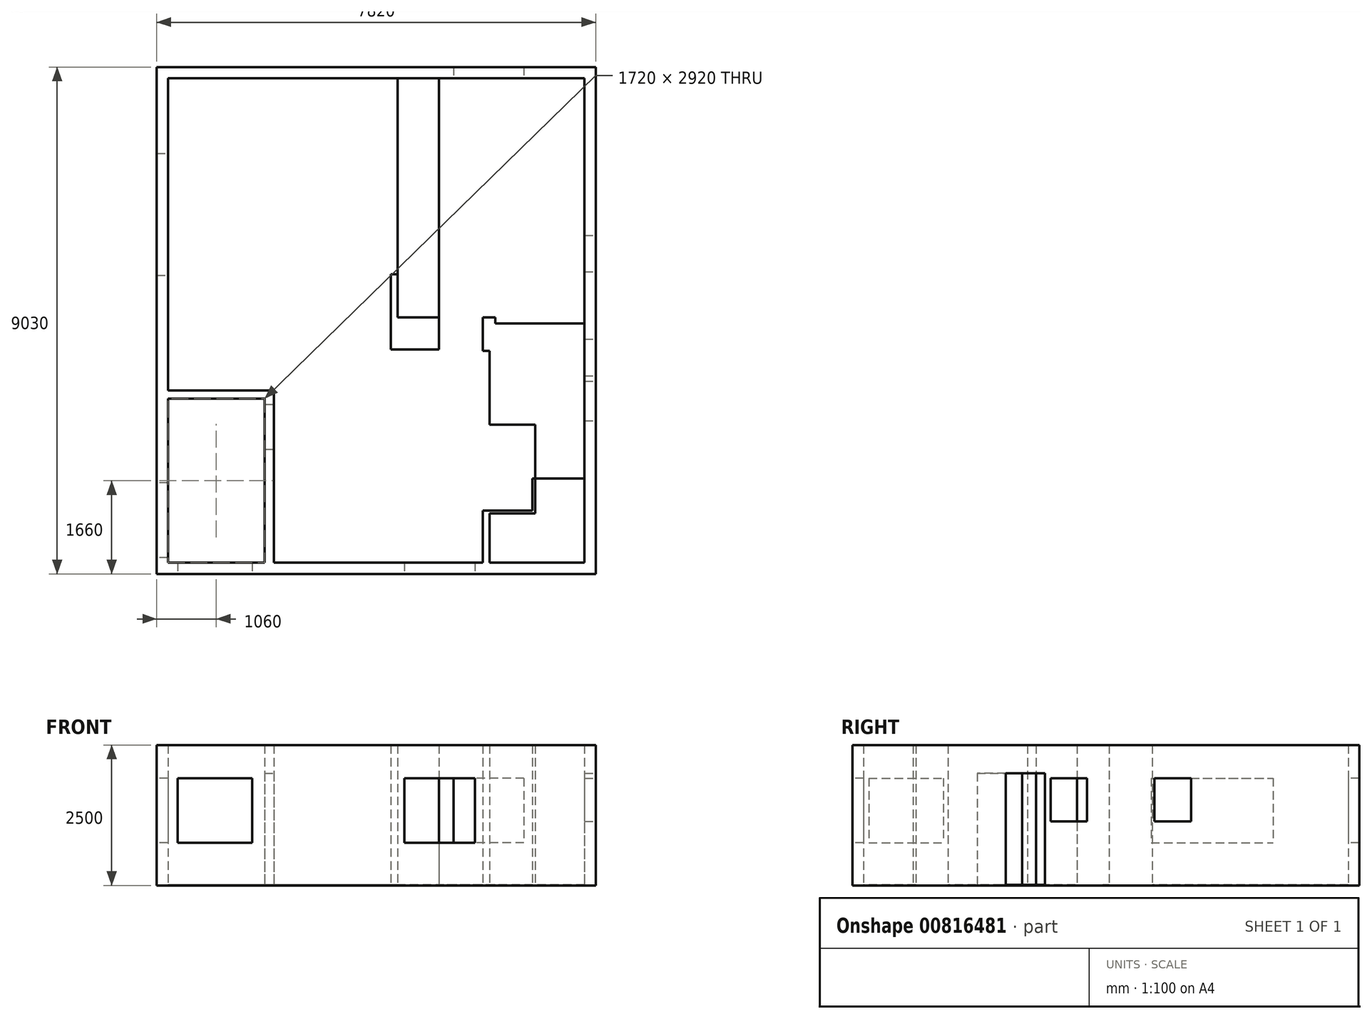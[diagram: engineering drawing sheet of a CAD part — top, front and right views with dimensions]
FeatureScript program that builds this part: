
annotation { "Feature Type Name" : "Feature", "Feature Type Description" : "" }
export const myFeature = defineFeature(function(context is Context, id is Id, definition is map)
    precondition{}
    {
        {
            var Q0;
            Q0=qCreatedBy(makeId("Top.planeOp"),FACE);
            var sketch = newSketch(context, id + "F0", { "sketchPlane" : qUnion([Q0])});
            skLineSegment(sketch, "E0.bottom", {"start": v(3710, -4315) * mm, "end": v(-3710, -4315) * mm});
            skLineSegment(sketch, "E0.top", {"start": v(3710, 4315) * mm, "end": v(-3710, 4315) * mm});
            skLineSegment(sketch, "E0.left", {"start": v(3710, -4315) * mm, "end": v(3710, 4315) * mm});
            skLineSegment(sketch, "E0.right", {"start": v(-3710, -4315) * mm, "end": v(-3710, 4315) * mm});
            skPoint(sketch, "E0.middle", {"position": v(0, 0) * mm});
            skLineSegment(sketch, "E1.0", {"start": v(3910, 4515) * mm, "end": v(-3910, 4515) * mm});
            skLineSegment(sketch, "E1.1", {"start": v(3910, -4515) * mm, "end": v(3910, 4515) * mm});
            skLineSegment(sketch, "E1.2", {"start": v(3910, -4515) * mm, "end": v(-3910, -4515) * mm});
            skLineSegment(sketch, "E1.3", {"start": v(-3910, -4515) * mm, "end": v(-3910, 4515) * mm});
            skLineSegment(sketch, "E2", {"start": v(380, 4315) * mm, "end": v(380, -515) * mm});
            skLineSegment(sketch, "E3", {"start": v(380, -515) * mm, "end": v(-3710, -515) * mm});
            skLineSegment(sketch, "E4.0", {"start": v(260, 4315) * mm, "end": v(260, -395) * mm});
            skLineSegment(sketch, "E5.0", {"start": v(260, -395) * mm, "end": v(-3710, -395) * mm});
            skLineSegment(sketch, "E6", {"start": v(3710, 55) * mm, "end": v(1900, 55) * mm});
            skLineSegment(sketch, "E7.0", {"start": v(3710, -55) * mm, "end": v(2020, -55) * mm});
            skLineSegment(sketch, "E8", {"start": v(2120, 105) * mm, "end": v(2120, -105) * mm});
            skLineSegment(sketch, "E9.0", {"start": v(2940, 105) * mm, "end": v(2940, -105) * mm});
            skLineSegment(sketch, "E10", {"start": v(3660, 865) * mm, "end": v(3960, 865) * mm});
            skLineSegment(sketch, "E11.0", {"start": v(3660, 1515) * mm, "end": v(3960, 1515) * mm});
            skLineSegment(sketch, "E12", {"start": v(2630, 4565) * mm, "end": v(2630, 4265) * mm});
            skLineSegment(sketch, "E13.0", {"start": v(1380, 4565) * mm, "end": v(1380, 4265) * mm});
            skLineSegment(sketch, "E14", {"start": v(210, 1645) * mm, "end": v(430, 1645) * mm});
            skLineSegment(sketch, "E15.0", {"start": v(210, 825) * mm, "end": v(430, 825) * mm});
            skLineSegment(sketch, "E16", {"start": v(3660, -335) * mm, "end": v(3960, -335) * mm});
            skLineSegment(sketch, "E17.0", {"start": v(3660, -985) * mm, "end": v(3960, -985) * mm});
            skLineSegment(sketch, "E18.0", {"start": v(3660, -1085) * mm, "end": v(3960, -1085) * mm});
            skLineSegment(sketch, "E19.0", {"start": v(3660, -1785) * mm, "end": v(3960, -1785) * mm});
            skLineSegment(sketch, "E20", {"start": v(3710, -2815) * mm, "end": v(2830, -2815) * mm});
            skLineSegment(sketch, "E21", {"start": v(2830, -2815) * mm, "end": v(2830, -3435) * mm});
            skLineSegment(sketch, "E22", {"start": v(-3960, 2975) * mm, "end": v(-3660, 2975) * mm});
            skLineSegment(sketch, "E23.0", {"start": v(-3960, 805) * mm, "end": v(-3660, 805) * mm});
            skLineSegment(sketch, "E24", {"start": v(-1560, -345) * mm, "end": v(-1560, -565) * mm});
            skLineSegment(sketch, "E25.0", {"start": v(-740, -345) * mm, "end": v(-740, -565) * mm});
            skLineSegment(sketch, "E26", {"start": v(-1820, -515) * mm, "end": v(-1820, -4315) * mm});
            skLineSegment(sketch, "E27", {"start": v(-3710, -1245) * mm, "end": v(-1820, -1245) * mm});
            skLineSegment(sketch, "E28.0", {"start": v(-3710, -1395) * mm, "end": v(-1990, -1395) * mm});
            skLineSegment(sketch, "E29", {"start": v(-3660, -2895) * mm, "end": v(-3960, -2895) * mm});
            skLineSegment(sketch, "E30.0", {"start": v(-3660, -4225) * mm, "end": v(-3960, -4225) * mm});
            skLineSegment(sketch, "E31", {"start": v(-2210, -4265) * mm, "end": v(-2210, -4565) * mm});
            skLineSegment(sketch, "E32.0", {"start": v(-3540, -4265) * mm, "end": v(-3540, -4565) * mm});
            skLineSegment(sketch, "E33", {"start": v(-1990, -4315) * mm, "end": v(-1990, -1395) * mm});
            skLineSegment(sketch, "E34", {"start": v(-1920, -515) * mm, "end": v(-1920, -1245) * mm});
            skLineSegment(sketch, "E35", {"start": v(-2040, -1495) * mm, "end": v(-1770, -1495) * mm});
            skLineSegment(sketch, "E36.0", {"start": v(-2040, -2295) * mm, "end": v(-1770, -2295) * mm});
            skLineSegment(sketch, "E37", {"start": v(-1770, -535) * mm, "end": v(-1970, -535) * mm});
            skLineSegment(sketch, "E38.0", {"start": v(-1770, -1135) * mm, "end": v(-1970, -1135) * mm});
            skLineSegment(sketch, "E39", {"start": v(2020, -55) * mm, "end": v(2020, -515) * mm});
            skLineSegment(sketch, "E40", {"start": v(1900, -515) * mm, "end": v(380, -515) * mm});
            skLineSegment(sketch, "E41", {"start": v(500, -4265) * mm, "end": v(500, -4565) * mm});
            skLineSegment(sketch, "E42.0", {"start": v(1760, -4265) * mm, "end": v(1760, -4565) * mm});
            skLineSegment(sketch, "E43", {"start": v(2020, -515) * mm, "end": v(2020, -4315) * mm});
            skLineSegment(sketch, "E44", {"start": v(2830, -3435) * mm, "end": v(2020, -3435) * mm});
            skLineSegment(sketch, "E45", {"start": v(2830, -3125) * mm, "end": v(3710, -3125) * mm});
            skLineSegment(sketch, "E46", {"start": v(2830, -3435) * mm, "end": v(3710, -3435) * mm});
            skLineSegment(sketch, "E47", {"start": v(2830, -3435) * mm, "end": v(2830, -4315) * mm});
            skLineSegment(sketch, "E48", {"start": v(2425, -3435) * mm, "end": v(2425, -4315) * mm});
            skLineSegment(sketch, "E49", {"start": v(2830, -3435) * mm, "end": v(3710, -4315) * mm});
            skLineSegment(sketch, "E50", {"start": v(2830, -3435) * mm, "end": v(3710, -3799.5) * mm});
            skLineSegment(sketch, "E51", {"start": v(2830, -3435) * mm, "end": v(3194.5, -4315) * mm});
            skLineSegment(sketch, "E52", {"start": v(1900, -4315) * mm, "end": v(1900, 55) * mm});
            skLineSegment(sketch, "E53", {"start": v(1850, -1365) * mm, "end": v(2070, -1365) * mm});
            skLineSegment(sketch, "E54.0", {"start": v(1850, -545) * mm, "end": v(2070, -545) * mm});
            skLineSegment(sketch, "E55", {"start": v(2020, -1855) * mm, "end": v(2830, -1855) * mm});
            skLineSegment(sketch, "E56", {"start": v(2830, -1855) * mm, "end": v(2830, -2815) * mm});
            skLineSegment(sketch, "E57.0", {"start": v(2020, -1905) * mm, "end": v(2780, -1905) * mm});
            skLineSegment(sketch, "E58.0", {"start": v(2780, -3385) * mm, "end": v(2020, -3385) * mm});
            skLineSegment(sketch, "E59", {"start": v(2780, -1905) * mm, "end": v(2780, -3385) * mm});
            skLineSegment(sketch, "E60", {"start": v(2880, -2565) * mm, "end": v(2730, -2565) * mm});
            skLineSegment(sketch, "E61.0", {"start": v(2880, -1915) * mm, "end": v(2730, -1915) * mm});
            skLineSegment(sketch, "E62", {"start": v(1900, -415) * mm, "end": v(1120, -415) * mm});
            skLineSegment(sketch, "E63.trimOffspring", {"start": v(1120, 55) * mm, "end": v(380, 55) * mm});
            skLineSegment(sketch, "E64", {"start": v(1120, 55) * mm, "end": v(1120, -515) * mm});
            skLineSegment(sketch, "E65", {"start": v(2830, -2815) * mm, "end": v(2780, -2815) * mm});
            skLineSegment(sketch, "E66", {"start": v(2020, -3385) * mm, "end": v(1900, -3385) * mm});
            skLineSegment(sketch, "E67", {"start": v(260, -395) * mm, "end": v(260, -515) * mm});
            skLineSegment(sketch, "E68", {"start": v(1120, 55) * mm, "end": v(1120, 4315) * mm});
            skSolve(sketch);
        }
        {
            var Q0;
            {var subQ0=sQuery(id+"F0.wireOp",EDGE,"E0.right");var subQ1=sQuery(id+"F0.wireOp",EDGE,"E0.top");var subQ2=makeQuery(id+"F0.imprint","INTERSECT",VERTEX,{"derivedFrom":[subQ1,subQ0]});Q0=makeQuery(id+"F0.imprint","IMPRINT",FACE,{"disambiguationData":[TD([[makeQuery(id+"F0.imprint","IMPRINT",EDGE,{"disambiguationData":[TD([[subQ2,1.0]])],"derivedFrom":subQ1}),1.0]])]});}
            var Q1;
            {var subQ0=sQuery(id+"F0.wireOp",EDGE,"E25.0");var subQ1=sQuery(id+"F0.wireOp",EDGE,"E3");var subQ2=makeQuery(id+"F0.imprint","INTERSECT",VERTEX,{"derivedFrom":[subQ1,subQ0]});Q1=makeQuery(id+"F0.imprint","IMPRINT",FACE,{"disambiguationData":[TD([[makeQuery(id+"F0.imprint","IMPRINT",EDGE,{"disambiguationData":[TD([[subQ2,-1.0]])],"derivedFrom":subQ1}),-1.0]])]});}
            var Q2;
            {var subQ1=sQuery(id+"F0.wireOp",EDGE,"E3");var subQ5=sQuery(id+"F0.wireOp",EDGE,"E0.right");var subQ9=makeQuery(id+"F0.imprint","INTERSECT",VERTEX,{"derivedFrom":[subQ5,subQ1]});Q2=makeQuery(id+"F0.imprint","IMPRINT",FACE,{"disambiguationData":[TD([[makeQuery(id+"F0.imprint","IMPRINT",EDGE,{"disambiguationData":[TD([[subQ9,1.0]])],"derivedFrom":subQ5}),-1.0]])]});}
            var Q3;
            {var subQ9=sQuery(id+"F0.wireOp",EDGE,"E52");var subQ12=sQuery(id+"F0.wireOp",EDGE,"E0.bottom");var subQ18=makeQuery(id+"F0.imprint","INTERSECT",VERTEX,{"derivedFrom":[subQ12,subQ9]});Q3=makeQuery(id+"F0.imprint","IMPRINT",FACE,{"disambiguationData":[TD([[makeQuery(id+"F0.imprint","IMPRINT",EDGE,{"disambiguationData":[TD([[subQ18,-1.0]])],"derivedFrom":subQ12}),-1.0]])]});}
            var Q4;
            {var subQ0=sQuery(id+"F0.wireOp",EDGE,"E35");var subQ1=sQuery(id+"F0.wireOp",EDGE,"E26");var subQ2=makeQuery(id+"F0.imprint","INTERSECT",VERTEX,{"derivedFrom":[subQ1,subQ0]});Q4=makeQuery(id+"F0.imprint","IMPRINT",FACE,{"disambiguationData":[TD([[makeQuery(id+"F0.imprint","IMPRINT",EDGE,{"disambiguationData":[TD([[subQ2,-1.0]])],"derivedFrom":subQ1}),-1.0]])]});}
            var Q5;
            {var subQ5=sQuery(id+"F0.wireOp",EDGE,"E28.0");Q5=makeQuery(id+"F0.imprint","IMPRINT",FACE,{"disambiguationData":[TD([[makeQuery(id+"F0.imprint","IMPRINT",EDGE,{"derivedFrom":subQ5}),-1.0]])]});}
            var Q6;
            {var subQ0=sQuery(id+"F0.wireOp",EDGE,"E54.0");var subQ1=sQuery(id+"F0.wireOp",EDGE,"E43");var subQ2=makeQuery(id+"F0.imprint","INTERSECT",VERTEX,{"derivedFrom":[subQ1,subQ0]});Q6=makeQuery(id+"F0.imprint","IMPRINT",FACE,{"disambiguationData":[TD([[makeQuery(id+"F0.imprint","IMPRINT",EDGE,{"disambiguationData":[TD([[subQ2,-1.0]])],"derivedFrom":subQ1}),-1.0]])]});}
            var Q7;
            {var subQ0=sQuery(id+"F0.wireOp",EDGE,"E20");Q7=makeQuery(id+"F0.imprint","IMPRINT",FACE,{"disambiguationData":[TD([[makeQuery(id+"F0.imprint","IMPRINT",EDGE,{"derivedFrom":subQ0}),-1.0]])]});}
            var Q8;
            {var subQ1=sQuery(id+"F0.wireOp",EDGE,"E57.0");Q8=makeQuery(id+"F0.imprint","IMPRINT",FACE,{"disambiguationData":[TD([[makeQuery(id+"F0.imprint","IMPRINT",EDGE,{"derivedFrom":subQ1}),-1.0]])]});}
            var Q9;
            {var subQ0=sQuery(id+"F0.wireOp",EDGE,"E9.0");var subQ1=sQuery(id+"F0.wireOp",EDGE,"E6");var subQ2=makeQuery(id+"F0.imprint","INTERSECT",VERTEX,{"derivedFrom":[subQ1,subQ0]});Q9=makeQuery(id+"F0.imprint","IMPRINT",FACE,{"disambiguationData":[TD([[makeQuery(id+"F0.imprint","IMPRINT",EDGE,{"disambiguationData":[TD([[subQ2,-1.0]])],"derivedFrom":subQ1}),1.0]])]});}
            var Q10;
            {var subQ0=sQuery(id+"F0.wireOp",EDGE,"E19.0");var subQ1=sQuery(id+"F0.wireOp",EDGE,"E0.left");var subQ2=makeQuery(id+"F0.imprint","INTERSECT",VERTEX,{"derivedFrom":[subQ1,subQ0]});Q10=makeQuery(id+"F0.imprint","IMPRINT",FACE,{"disambiguationData":[TD([[makeQuery(id+"F0.imprint","IMPRINT",EDGE,{"disambiguationData":[TD([[subQ2,-1.0]])],"derivedFrom":subQ1}),-1.0]])]});}
            var Q11;
            {var subQ18=sQuery(id+"F0.wireOp",EDGE,"E62");Q11=makeQuery(id+"F0.imprint","IMPRINT",FACE,{"disambiguationData":[TD([[makeQuery(id+"F0.imprint","IMPRINT",EDGE,{"derivedFrom":subQ18}),-1.0]])]});}
            var Q12;
            {var subQ0=sQuery(id+"F0.wireOp",EDGE,"E14");var subQ1=sQuery(id+"F0.wireOp",EDGE,"E2");var subQ2=makeQuery(id+"F0.imprint","INTERSECT",VERTEX,{"derivedFrom":[subQ1,subQ0]});Q12=makeQuery(id+"F0.imprint","IMPRINT",FACE,{"disambiguationData":[TD([[makeQuery(id+"F0.imprint","IMPRINT",EDGE,{"disambiguationData":[TD([[subQ2,-1.0]])],"derivedFrom":subQ1}),-1.0]])]});}
            var Q13;
            {var subQ0=sQuery(id+"F0.wireOp",EDGE,"E20");Q13=makeQuery(id+"F0.imprint","IMPRINT",FACE,{"disambiguationData":[TD([[makeQuery(id+"F0.imprint","IMPRINT",EDGE,{"derivedFrom":subQ0}),1.0]])]});}
            var Q14;
            {var subQ0=sQuery(id+"F0.wireOp",EDGE,"E45");Q14=makeQuery(id+"F0.imprint","IMPRINT",FACE,{"disambiguationData":[TD([[makeQuery(id+"F0.imprint","IMPRINT",EDGE,{"derivedFrom":subQ0}),-1.0]])]});}
            var Q15;
            {var subQ0=sQuery(id+"F0.wireOp",EDGE,"E46");Q15=makeQuery(id+"F0.imprint","IMPRINT",FACE,{"disambiguationData":[TD([[makeQuery(id+"F0.imprint","IMPRINT",EDGE,{"derivedFrom":subQ0}),-1.0]])]});}
            var Q16;
            {var subQ0=sQuery(id+"F0.wireOp",EDGE,"E49");Q16=makeQuery(id+"F0.imprint","IMPRINT",FACE,{"disambiguationData":[TD([[makeQuery(id+"F0.imprint","IMPRINT",EDGE,{"derivedFrom":subQ0}),1.0]])]});}
            var Q17;
            {var subQ0=sQuery(id+"F0.wireOp",EDGE,"E49");Q17=makeQuery(id+"F0.imprint","IMPRINT",FACE,{"disambiguationData":[TD([[makeQuery(id+"F0.imprint","IMPRINT",EDGE,{"derivedFrom":subQ0}),-1.0]])]});}
            var Q18;
            {var subQ0=sQuery(id+"F0.wireOp",EDGE,"E47");Q18=makeQuery(id+"F0.imprint","IMPRINT",FACE,{"disambiguationData":[TD([[makeQuery(id+"F0.imprint","IMPRINT",EDGE,{"derivedFrom":subQ0}),1.0]])]});}
            var Q19;
            {var subQ0=sQuery(id+"F0.wireOp",EDGE,"E47");Q19=makeQuery(id+"F0.imprint","IMPRINT",FACE,{"disambiguationData":[TD([[makeQuery(id+"F0.imprint","IMPRINT",EDGE,{"derivedFrom":subQ0}),-1.0]])]});}
            var Q20;
            {var subQ3=sQuery(id+"F0.wireOp",EDGE,"E48");Q20=makeQuery(id+"F0.imprint","IMPRINT",FACE,{"disambiguationData":[TD([[makeQuery(id+"F0.imprint","IMPRINT",EDGE,{"derivedFrom":subQ3}),-1.0]])]});}
            var Q21;
            {var subQ2=sQuery(id+"F0.wireOp",EDGE,"E66");Q21=makeQuery(id+"F0.imprint","IMPRINT",FACE,{"disambiguationData":[TD([[makeQuery(id+"F0.imprint","IMPRINT",EDGE,{"derivedFrom":subQ2}),-1.0]])]});}
            var Q22;
            {var subQ0=sQuery(id+"F0.wireOp",EDGE,"E6");var subQ1=sQuery(id+"F0.wireOp",EDGE,"E0.left");var subQ2=makeQuery(id+"F0.imprint","INTERSECT",VERTEX,{"derivedFrom":[subQ1,subQ0]});Q22=makeQuery(id+"F0.imprint","IMPRINT",FACE,{"disambiguationData":[TD([[makeQuery(id+"F0.imprint","IMPRINT",EDGE,{"disambiguationData":[TD([[subQ2,1.0]])],"derivedFrom":subQ1}),1.0]])]});}
            var Q23;
            {var subQ2=sQuery(id+"F0.wireOp",EDGE,"E66");Q23=makeQuery(id+"F0.imprint","IMPRINT",FACE,{"disambiguationData":[TD([[makeQuery(id+"F0.imprint","IMPRINT",EDGE,{"derivedFrom":subQ2}),1.0]])]});}
            var Q24;
            {var subQ0=sQuery(id+"F0.wireOp",EDGE,"E39");Q24=makeQuery(id+"F0.imprint","IMPRINT",FACE,{"disambiguationData":[TD([[makeQuery(id+"F0.imprint","IMPRINT",EDGE,{"derivedFrom":subQ0}),-1.0]])]});}
            var Q25;
            {var subQ5=sQuery(id+"F0.wireOp",EDGE,"E62");Q25=makeQuery(id+"F0.imprint","IMPRINT",FACE,{"disambiguationData":[TD([[makeQuery(id+"F0.imprint","IMPRINT",EDGE,{"derivedFrom":subQ5}),1.0]])]});}
            var Q26;
            {var subQ2=sQuery(id+"F0.wireOp",EDGE,"E63.trimOffspring");Q26=makeQuery(id+"F0.imprint","IMPRINT",FACE,{"disambiguationData":[TD([[makeQuery(id+"F0.imprint","IMPRINT",EDGE,{"derivedFrom":subQ2}),1.0]])]});}
            var Q27;
            {var subQ3=sQuery(id+"F0.wireOp",EDGE,"E67");Q27=makeQuery(id+"F0.imprint","IMPRINT",FACE,{"disambiguationData":[TD([[makeQuery(id+"F0.imprint","IMPRINT",EDGE,{"derivedFrom":subQ3}),1.0]])]});}
            var Q28;
            {var subQ0=sQuery(id+"F0.wireOp",EDGE,"E67");Q28=makeQuery(id+"F0.imprint","IMPRINT",FACE,{"disambiguationData":[TD([[makeQuery(id+"F0.imprint","IMPRINT",EDGE,{"derivedFrom":subQ0}),-1.0]])]});}
            var Q29;
            {var subQ0=sQuery(id+"F0.wireOp",EDGE,"E2");var subQ1=sQuery(id+"F0.wireOp",EDGE,"E0.top");var subQ2=makeQuery(id+"F0.imprint","INTERSECT",VERTEX,{"derivedFrom":[subQ1,subQ0]});Q29=makeQuery(id+"F0.imprint","IMPRINT",FACE,{"disambiguationData":[TD([[makeQuery(id+"F0.imprint","IMPRINT",EDGE,{"disambiguationData":[TD([[subQ2,-1.0]])],"derivedFrom":subQ1}),1.0]])]});}
            var Q30;
            {var subQ0=sQuery(id+"F0.wireOp",EDGE,"E26");var subQ1=sQuery(id+"F0.wireOp",EDGE,"E0.bottom");var subQ2=makeQuery(id+"F0.imprint","INTERSECT",VERTEX,{"derivedFrom":[subQ1,subQ0]});Q30=makeQuery(id+"F0.imprint","IMPRINT",FACE,{"disambiguationData":[TD([[makeQuery(id+"F0.imprint","IMPRINT",EDGE,{"disambiguationData":[TD([[subQ2,-1.0]])],"derivedFrom":subQ1}),-1.0]])]});}
            var Q31;
            {var subQ1=sQuery(id+"F0.wireOp",EDGE,"E55");Q31=makeQuery(id+"F0.imprint","IMPRINT",FACE,{"disambiguationData":[TD([[makeQuery(id+"F0.imprint","IMPRINT",EDGE,{"derivedFrom":subQ1}),-1.0]])]});}
            var Q32;
            {var subQ0=sQuery(id+"F0.wireOp",EDGE,"E61.0");var subQ1=sQuery(id+"F0.wireOp",EDGE,"E56");var subQ2=makeQuery(id+"F0.imprint","INTERSECT",VERTEX,{"derivedFrom":[subQ1,subQ0]});Q32=makeQuery(id+"F0.imprint","IMPRINT",FACE,{"disambiguationData":[TD([[makeQuery(id+"F0.imprint","IMPRINT",EDGE,{"disambiguationData":[TD([[subQ2,-1.0]])],"derivedFrom":subQ1}),-1.0]])]});}
            var Q33;
            {var subQ0=sQuery(id+"F0.wireOp",EDGE,"E65");Q33=makeQuery(id+"F0.imprint","IMPRINT",FACE,{"disambiguationData":[TD([[makeQuery(id+"F0.imprint","IMPRINT",EDGE,{"derivedFrom":subQ0}),-1.0]])]});}
            var Q34;
            {var subQ3=sQuery(id+"F0.wireOp",EDGE,"E58.0");Q34=makeQuery(id+"F0.imprint","IMPRINT",FACE,{"disambiguationData":[TD([[makeQuery(id+"F0.imprint","IMPRINT",EDGE,{"derivedFrom":subQ3}),1.0]])]});}
            var Q35;
            {var subQ8=sQuery(id+"F0.wireOp",EDGE,"E28.0");Q35=makeQuery(id+"F0.imprint","IMPRINT",FACE,{"disambiguationData":[TD([[makeQuery(id+"F0.imprint","IMPRINT",EDGE,{"derivedFrom":subQ8}),1.0]])]});}
            var Q36;
            {var subQ0=sQuery(id+"F0.wireOp",EDGE,"E27");var subQ1=sQuery(id+"F0.wireOp",EDGE,"E26");var subQ2=makeQuery(id+"F0.imprint","INTERSECT",VERTEX,{"derivedFrom":[subQ1,subQ0]});Q36=makeQuery(id+"F0.imprint","IMPRINT",FACE,{"disambiguationData":[TD([[makeQuery(id+"F0.imprint","IMPRINT",EDGE,{"disambiguationData":[TD([[subQ2,1.0]])],"derivedFrom":subQ1}),-1.0]])]});}
            var Q37;
            {var subQ0=sQuery(id+"F0.wireOp",EDGE,"E37");var subQ1=sQuery(id+"F0.wireOp",EDGE,"E26");var subQ2=makeQuery(id+"F0.imprint","INTERSECT",VERTEX,{"derivedFrom":[subQ1,subQ0]});Q37=makeQuery(id+"F0.imprint","IMPRINT",FACE,{"disambiguationData":[TD([[makeQuery(id+"F0.imprint","IMPRINT",EDGE,{"disambiguationData":[TD([[subQ2,-1.0]])],"derivedFrom":subQ1}),-1.0]])]});}
            var Q38;
            {var subQ0=sQuery(id+"F0.wireOp",EDGE,"E26");var subQ1=sQuery(id+"F0.wireOp",EDGE,"E3");var subQ2=makeQuery(id+"F0.imprint","INTERSECT",VERTEX,{"derivedFrom":[subQ1,subQ0]});Q38=makeQuery(id+"F0.imprint","IMPRINT",FACE,{"disambiguationData":[TD([[makeQuery(id+"F0.imprint","IMPRINT",EDGE,{"disambiguationData":[TD([[subQ2,-1.0]])],"derivedFrom":subQ1}),1.0]])]});}
            var Q39;
            {var subQ0=sQuery(id+"F0.wireOp",EDGE,"E3");var subQ1=sQuery(id+"F0.wireOp",EDGE,"E0.right");var subQ2=makeQuery(id+"F0.imprint","INTERSECT",VERTEX,{"derivedFrom":[subQ1,subQ0]});Q39=makeQuery(id+"F0.imprint","IMPRINT",FACE,{"disambiguationData":[TD([[makeQuery(id+"F0.imprint","IMPRINT",EDGE,{"disambiguationData":[TD([[subQ2,-1.0]])],"derivedFrom":subQ1}),-1.0]])]});}
            extrude(context, id + "F1", {"entities" : qUnion([Q0, Q1, Q2, Q3, Q4, Q5, Q6, Q7, Q8, Q9, Q10, Q11, Q12, Q13, Q14, Q15, Q16, Q17, Q18, Q19, Q20, Q21, Q22, Q23, Q24, Q25, Q26, Q27, Q28, Q29, Q30, Q31, Q32, Q33, Q34, Q35, Q36, Q37, Q38, Q39]), "depth" : 10 * mm, "offsetDistance" : 25 * mm});
        }
        {
            var Q0;
            {var subQ1=sQuery(id+"F0.wireOp",EDGE,"E0.top");var subQ6=makeQuery(id+"F0.imprint","INTERSECT",VERTEX,{"derivedFrom":[subQ1,sQuery(id+"F0.wireOp",EDGE,"E2")]});Q0=makeQuery(id+"F0.imprint","IMPRINT",FACE,{"disambiguationData":[TD([[makeQuery(id+"F0.imprint","IMPRINT",EDGE,{"disambiguationData":[TD([[subQ6,1.0]])],"derivedFrom":subQ1}),-1.0]])]});}
            var Q1;
            {var subQ0=sQuery(id+"F0.wireOp",EDGE,"E12");var subQ1=sQuery(id+"F0.wireOp",EDGE,"E0.top");var subQ2=makeQuery(id+"F0.imprint","INTERSECT",VERTEX,{"derivedFrom":[subQ1,subQ0]});Q1=makeQuery(id+"F0.imprint","IMPRINT",FACE,{"disambiguationData":[TD([[makeQuery(id+"F0.imprint","IMPRINT",EDGE,{"disambiguationData":[TD([[subQ2,-1.0]])],"derivedFrom":subQ1}),-1.0]])]});}
            var Q2;
            {var subQ7=sQuery(id+"F0.wireOp",EDGE,"E0.left");var subQ9=sQuery(id+"F0.wireOp",EDGE,"E0.top");var subQ10=makeQuery(id+"F0.imprint","INTERSECT",VERTEX,{"derivedFrom":[subQ9,subQ7]});Q2=makeQuery(id+"F0.imprint","IMPRINT",FACE,{"disambiguationData":[TD([[makeQuery(id+"F0.imprint","IMPRINT",EDGE,{"disambiguationData":[TD([[subQ10,-1.0]])],"derivedFrom":subQ9}),-1.0]])]});}
            var Q3;
            {var subQ0=sQuery(id+"F0.wireOp",EDGE,"E10");var subQ1=sQuery(id+"F0.wireOp",EDGE,"E0.left");var subQ2=makeQuery(id+"F0.imprint","INTERSECT",VERTEX,{"derivedFrom":[subQ1,subQ0]});Q3=makeQuery(id+"F0.imprint","IMPRINT",FACE,{"disambiguationData":[TD([[makeQuery(id+"F0.imprint","IMPRINT",EDGE,{"disambiguationData":[TD([[subQ2,-1.0]])],"derivedFrom":subQ1}),-1.0]])]});}
            var Q4;
            {var subQ0=sQuery(id+"F0.wireOp",EDGE,"E0.left");var subQ8=makeQuery(id+"F0.imprint","INTERSECT",VERTEX,{"derivedFrom":[subQ0,sQuery(id+"F0.wireOp",EDGE,"E7.0")]});Q4=makeQuery(id+"F0.imprint","IMPRINT",FACE,{"disambiguationData":[TD([[makeQuery(id+"F0.imprint","IMPRINT",EDGE,{"disambiguationData":[TD([[subQ8,1.0]])],"derivedFrom":subQ0}),-1.0]])]});}
            var Q5;
            {var subQ0=sQuery(id+"F0.wireOp",EDGE,"E17.0");var subQ1=sQuery(id+"F0.wireOp",EDGE,"E0.left");var subQ2=makeQuery(id+"F0.imprint","INTERSECT",VERTEX,{"derivedFrom":[subQ1,subQ0]});Q5=makeQuery(id+"F0.imprint","IMPRINT",FACE,{"disambiguationData":[TD([[makeQuery(id+"F0.imprint","IMPRINT",EDGE,{"disambiguationData":[TD([[subQ2,-1.0]])],"derivedFrom":subQ1}),-1.0]])]});}
            var Q6;
            {var subQ0=sQuery(id+"F0.wireOp",EDGE,"E18.0");var subQ1=sQuery(id+"F0.wireOp",EDGE,"E0.left");var subQ2=makeQuery(id+"F0.imprint","INTERSECT",VERTEX,{"derivedFrom":[subQ1,subQ0]});Q6=makeQuery(id+"F0.imprint","IMPRINT",FACE,{"disambiguationData":[TD([[makeQuery(id+"F0.imprint","IMPRINT",EDGE,{"disambiguationData":[TD([[subQ2,-1.0]])],"derivedFrom":subQ1}),-1.0]])]});}
            var Q7;
            {var subQ0=sQuery(id+"F0.wireOp",EDGE,"E19.0");var subQ1=sQuery(id+"F0.wireOp",EDGE,"E0.left");var subQ2=makeQuery(id+"F0.imprint","INTERSECT",VERTEX,{"derivedFrom":[subQ1,subQ0]});Q7=makeQuery(id+"F0.imprint","IMPRINT",FACE,{"disambiguationData":[TD([[makeQuery(id+"F0.imprint","IMPRINT",EDGE,{"disambiguationData":[TD([[subQ2,-1.0]])],"derivedFrom":subQ1}),-1.0]])]});}
            var Q8;
            {var subQ10=sQuery(id+"F0.wireOp",EDGE,"E0.bottom");var subQ17=makeQuery(id+"F0.imprint","INTERSECT",VERTEX,{"derivedFrom":[subQ10,sQuery(id+"F0.wireOp",EDGE,"E47")]});Q8=makeQuery(id+"F0.imprint","IMPRINT",FACE,{"disambiguationData":[TD([[makeQuery(id+"F0.imprint","IMPRINT",EDGE,{"disambiguationData":[TD([[subQ17,1.0]])],"derivedFrom":subQ10}),1.0]])]});}
            var Q9;
            {var subQ0=sQuery(id+"F0.wireOp",EDGE,"E42.0");var subQ1=sQuery(id+"F0.wireOp",EDGE,"E0.bottom");var subQ2=makeQuery(id+"F0.imprint","INTERSECT",VERTEX,{"derivedFrom":[subQ1,subQ0]});Q9=makeQuery(id+"F0.imprint","IMPRINT",FACE,{"disambiguationData":[TD([[makeQuery(id+"F0.imprint","IMPRINT",EDGE,{"disambiguationData":[TD([[subQ2,-1.0]])],"derivedFrom":subQ1}),1.0]])]});}
            var Q10;
            {var subQ5=sQuery(id+"F0.wireOp",EDGE,"E0.bottom");var subQ6=makeQuery(id+"F0.imprint","INTERSECT",VERTEX,{"derivedFrom":[subQ5,sQuery(id+"F0.wireOp",EDGE,"E26")]});Q10=makeQuery(id+"F0.imprint","IMPRINT",FACE,{"disambiguationData":[TD([[makeQuery(id+"F0.imprint","IMPRINT",EDGE,{"disambiguationData":[TD([[subQ6,1.0]])],"derivedFrom":subQ5}),1.0]])]});}
            var Q11;
            {var subQ0=sQuery(id+"F0.wireOp",EDGE,"E31");var subQ1=sQuery(id+"F0.wireOp",EDGE,"E0.bottom");var subQ2=makeQuery(id+"F0.imprint","INTERSECT",VERTEX,{"derivedFrom":[subQ1,subQ0]});Q11=makeQuery(id+"F0.imprint","IMPRINT",FACE,{"disambiguationData":[TD([[makeQuery(id+"F0.imprint","IMPRINT",EDGE,{"disambiguationData":[TD([[subQ2,-1.0]])],"derivedFrom":subQ1}),1.0]])]});}
            var Q12;
            {var subQ5=sQuery(id+"F0.wireOp",EDGE,"E0.right");var subQ9=sQuery(id+"F0.wireOp",EDGE,"E0.bottom");var subQ10=makeQuery(id+"F0.imprint","INTERSECT",VERTEX,{"derivedFrom":[subQ9,subQ5]});Q12=makeQuery(id+"F0.imprint","IMPRINT",FACE,{"disambiguationData":[TD([[makeQuery(id+"F0.imprint","IMPRINT",EDGE,{"disambiguationData":[TD([[subQ10,1.0]])],"derivedFrom":subQ9}),1.0]])]});}
            var Q13;
            {var subQ0=sQuery(id+"F0.wireOp",EDGE,"E30.0");var subQ1=sQuery(id+"F0.wireOp",EDGE,"E0.right");var subQ2=makeQuery(id+"F0.imprint","INTERSECT",VERTEX,{"derivedFrom":[subQ1,subQ0]});Q13=makeQuery(id+"F0.imprint","IMPRINT",FACE,{"disambiguationData":[TD([[makeQuery(id+"F0.imprint","IMPRINT",EDGE,{"disambiguationData":[TD([[subQ2,-1.0]])],"derivedFrom":subQ1}),1.0]])]});}
            var Q14;
            {var subQ0=sQuery(id+"F0.wireOp",EDGE,"E0.right");var subQ9=makeQuery(id+"F0.imprint","INTERSECT",VERTEX,{"derivedFrom":[subQ0,sQuery(id+"F0.wireOp",EDGE,"E28.0")]});Q14=makeQuery(id+"F0.imprint","IMPRINT",FACE,{"disambiguationData":[TD([[makeQuery(id+"F0.imprint","IMPRINT",EDGE,{"disambiguationData":[TD([[subQ9,1.0]])],"derivedFrom":subQ0}),1.0]])]});}
            var Q15;
            {var subQ0=sQuery(id+"F0.wireOp",EDGE,"E23.0");var subQ1=sQuery(id+"F0.wireOp",EDGE,"E0.right");var subQ2=makeQuery(id+"F0.imprint","INTERSECT",VERTEX,{"derivedFrom":[subQ1,subQ0]});Q15=makeQuery(id+"F0.imprint","IMPRINT",FACE,{"disambiguationData":[TD([[makeQuery(id+"F0.imprint","IMPRINT",EDGE,{"disambiguationData":[TD([[subQ2,-1.0]])],"derivedFrom":subQ1}),1.0]])]});}
            var Q16;
            {var subQ2=sQuery(id+"F0.wireOp",EDGE,"E63.trimOffspring");Q16=makeQuery(id+"F0.imprint","IMPRINT",FACE,{"disambiguationData":[TD([[makeQuery(id+"F0.imprint","IMPRINT",EDGE,{"derivedFrom":subQ2}),1.0]])]});}
            var Q17;
            {var subQ0=sQuery(id+"F0.wireOp",EDGE,"E26");var subQ1=sQuery(id+"F0.wireOp",EDGE,"E0.bottom");var subQ2=makeQuery(id+"F0.imprint","INTERSECT",VERTEX,{"derivedFrom":[subQ1,subQ0]});Q17=makeQuery(id+"F0.imprint","IMPRINT",FACE,{"disambiguationData":[TD([[makeQuery(id+"F0.imprint","IMPRINT",EDGE,{"disambiguationData":[TD([[subQ2,-1.0]])],"derivedFrom":subQ1}),-1.0]])]});}
            var Q18;
            {var subQ0=sQuery(id+"F0.wireOp",EDGE,"E35");var subQ1=sQuery(id+"F0.wireOp",EDGE,"E26");var subQ2=makeQuery(id+"F0.imprint","INTERSECT",VERTEX,{"derivedFrom":[subQ1,subQ0]});Q18=makeQuery(id+"F0.imprint","IMPRINT",FACE,{"disambiguationData":[TD([[makeQuery(id+"F0.imprint","IMPRINT",EDGE,{"disambiguationData":[TD([[subQ2,-1.0]])],"derivedFrom":subQ1}),-1.0]])]});}
            var Q19;
            {var subQ8=sQuery(id+"F0.wireOp",EDGE,"E28.0");Q19=makeQuery(id+"F0.imprint","IMPRINT",FACE,{"disambiguationData":[TD([[makeQuery(id+"F0.imprint","IMPRINT",EDGE,{"derivedFrom":subQ8}),1.0]])]});}
            var Q20;
            {var subQ3=sQuery(id+"F0.wireOp",EDGE,"E66");Q20=makeQuery(id+"F0.imprint","IMPRINT",FACE,{"disambiguationData":[TD([[makeQuery(id+"F0.imprint","IMPRINT",EDGE,{"derivedFrom":subQ3}),1.0]])]});}
            var Q21;
            {var subQ3=sQuery(id+"F0.wireOp",EDGE,"E58.0");Q21=makeQuery(id+"F0.imprint","IMPRINT",FACE,{"disambiguationData":[TD([[makeQuery(id+"F0.imprint","IMPRINT",EDGE,{"derivedFrom":subQ3}),1.0]])]});}
            var Q22;
            {var subQ3=sQuery(id+"F0.wireOp",EDGE,"E67");Q22=makeQuery(id+"F0.imprint","IMPRINT",FACE,{"disambiguationData":[TD([[makeQuery(id+"F0.imprint","IMPRINT",EDGE,{"derivedFrom":subQ3}),1.0]])]});}
            extrude(context, id + "F2", {"entities" : qUnion([Q0, Q1, Q2, Q3, Q4, Q5, Q6, Q7, Q8, Q9, Q10, Q11, Q12, Q13, Q14, Q15, Q16, Q17, Q18, Q19, Q20, Q21, Q22]), "operationType" : NewBodyOperationType.ADD, "depth" : 2500 * mm, "offsetDistance" : 25 * mm});
        }
        {
            var Q0;
            {var subQ0=sQuery(id+"F0.wireOp",EDGE,"E9.0");var subQ1=sQuery(id+"F0.wireOp",EDGE,"E6");var subQ2=makeQuery(id+"F0.imprint","INTERSECT",VERTEX,{"derivedFrom":[subQ1,subQ0]});Q0=makeQuery(id+"F0.imprint","IMPRINT",FACE,{"disambiguationData":[TD([[makeQuery(id+"F0.imprint","IMPRINT",EDGE,{"disambiguationData":[TD([[subQ2,-1.0]])],"derivedFrom":subQ1}),1.0]])]});}
            var Q1;
            {var subQ0=sQuery(id+"F0.wireOp",EDGE,"E54.0");var subQ1=sQuery(id+"F0.wireOp",EDGE,"E43");var subQ2=makeQuery(id+"F0.imprint","INTERSECT",VERTEX,{"derivedFrom":[subQ1,subQ0]});Q1=makeQuery(id+"F0.imprint","IMPRINT",FACE,{"disambiguationData":[TD([[makeQuery(id+"F0.imprint","IMPRINT",EDGE,{"disambiguationData":[TD([[subQ2,-1.0]])],"derivedFrom":subQ1}),-1.0]])]});}
            var Q2;
            {var subQ0=sQuery(id+"F0.wireOp",EDGE,"E14");var subQ1=sQuery(id+"F0.wireOp",EDGE,"E2");var subQ2=makeQuery(id+"F0.imprint","INTERSECT",VERTEX,{"derivedFrom":[subQ1,subQ0]});Q2=makeQuery(id+"F0.imprint","IMPRINT",FACE,{"disambiguationData":[TD([[makeQuery(id+"F0.imprint","IMPRINT",EDGE,{"disambiguationData":[TD([[subQ2,-1.0]])],"derivedFrom":subQ1}),-1.0]])]});}
            var Q3;
            {var subQ0=sQuery(id+"F0.wireOp",EDGE,"E25.0");var subQ1=sQuery(id+"F0.wireOp",EDGE,"E3");var subQ2=makeQuery(id+"F0.imprint","INTERSECT",VERTEX,{"derivedFrom":[subQ1,subQ0]});Q3=makeQuery(id+"F0.imprint","IMPRINT",FACE,{"disambiguationData":[TD([[makeQuery(id+"F0.imprint","IMPRINT",EDGE,{"disambiguationData":[TD([[subQ2,-1.0]])],"derivedFrom":subQ1}),-1.0]])]});}
            var Q4;
            {var subQ0=sQuery(id+"F0.wireOp",EDGE,"E37");var subQ1=sQuery(id+"F0.wireOp",EDGE,"E26");var subQ2=makeQuery(id+"F0.imprint","INTERSECT",VERTEX,{"derivedFrom":[subQ1,subQ0]});Q4=makeQuery(id+"F0.imprint","IMPRINT",FACE,{"disambiguationData":[TD([[makeQuery(id+"F0.imprint","IMPRINT",EDGE,{"disambiguationData":[TD([[subQ2,-1.0]])],"derivedFrom":subQ1}),-1.0]])]});}
            var Q5;
            {var subQ0=sQuery(id+"F0.wireOp",EDGE,"E35");var subQ1=sQuery(id+"F0.wireOp",EDGE,"E26");var subQ2=makeQuery(id+"F0.imprint","INTERSECT",VERTEX,{"derivedFrom":[subQ1,subQ0]});Q5=makeQuery(id+"F0.imprint","IMPRINT",FACE,{"disambiguationData":[TD([[makeQuery(id+"F0.imprint","IMPRINT",EDGE,{"disambiguationData":[TD([[subQ2,-1.0]])],"derivedFrom":subQ1}),-1.0]])]});}
            var Q6;
            {var subQ0=sQuery(id+"F0.wireOp",EDGE,"E19.0");var subQ1=sQuery(id+"F0.wireOp",EDGE,"E0.left");var subQ2=makeQuery(id+"F0.imprint","INTERSECT",VERTEX,{"derivedFrom":[subQ1,subQ0]});Q6=makeQuery(id+"F0.imprint","IMPRINT",FACE,{"disambiguationData":[TD([[makeQuery(id+"F0.imprint","IMPRINT",EDGE,{"disambiguationData":[TD([[subQ2,-1.0]])],"derivedFrom":subQ1}),-1.0]])]});}
            var Q7;
            {var subQ0=sQuery(id+"F0.wireOp",EDGE,"E61.0");var subQ1=sQuery(id+"F0.wireOp",EDGE,"E56");var subQ2=makeQuery(id+"F0.imprint","INTERSECT",VERTEX,{"derivedFrom":[subQ1,subQ0]});Q7=makeQuery(id+"F0.imprint","IMPRINT",FACE,{"disambiguationData":[TD([[makeQuery(id+"F0.imprint","IMPRINT",EDGE,{"disambiguationData":[TD([[subQ2,-1.0]])],"derivedFrom":subQ1}),-1.0]])]});}
            extrude(context, id + "F3", {"entities" : qUnion([Q0, Q1, Q2, Q3, Q4, Q5, Q6, Q7]), "operationType" : NewBodyOperationType.REMOVE, "depth" : 2000 * mm, "offsetDistance" : 25 * mm, "hasSecondDirection" : true, "secondDirectionOppositeDirection" : false, "secondDirectionDepth" : 10 * mm});
        }
        {
            var Q0;
            {var subQ0=sQuery(id+"F0.wireOp",EDGE,"E12");var subQ1=sQuery(id+"F0.wireOp",EDGE,"E0.top");var subQ2=makeQuery(id+"F0.imprint","INTERSECT",VERTEX,{"derivedFrom":[subQ1,subQ0]});Q0=makeQuery(id+"F0.imprint","IMPRINT",FACE,{"disambiguationData":[TD([[makeQuery(id+"F0.imprint","IMPRINT",EDGE,{"disambiguationData":[TD([[subQ2,-1.0]])],"derivedFrom":subQ1}),-1.0]])]});}
            var Q1;
            {var subQ0=sQuery(id+"F0.wireOp",EDGE,"E23.0");var subQ1=sQuery(id+"F0.wireOp",EDGE,"E0.right");var subQ2=makeQuery(id+"F0.imprint","INTERSECT",VERTEX,{"derivedFrom":[subQ1,subQ0]});Q1=makeQuery(id+"F0.imprint","IMPRINT",FACE,{"disambiguationData":[TD([[makeQuery(id+"F0.imprint","IMPRINT",EDGE,{"disambiguationData":[TD([[subQ2,-1.0]])],"derivedFrom":subQ1}),1.0]])]});}
            var Q2;
            {var subQ0=sQuery(id+"F0.wireOp",EDGE,"E30.0");var subQ1=sQuery(id+"F0.wireOp",EDGE,"E0.right");var subQ2=makeQuery(id+"F0.imprint","INTERSECT",VERTEX,{"derivedFrom":[subQ1,subQ0]});Q2=makeQuery(id+"F0.imprint","IMPRINT",FACE,{"disambiguationData":[TD([[makeQuery(id+"F0.imprint","IMPRINT",EDGE,{"disambiguationData":[TD([[subQ2,-1.0]])],"derivedFrom":subQ1}),1.0]])]});}
            var Q3;
            {var subQ0=sQuery(id+"F0.wireOp",EDGE,"E31");var subQ1=sQuery(id+"F0.wireOp",EDGE,"E0.bottom");var subQ2=makeQuery(id+"F0.imprint","INTERSECT",VERTEX,{"derivedFrom":[subQ1,subQ0]});Q3=makeQuery(id+"F0.imprint","IMPRINT",FACE,{"disambiguationData":[TD([[makeQuery(id+"F0.imprint","IMPRINT",EDGE,{"disambiguationData":[TD([[subQ2,-1.0]])],"derivedFrom":subQ1}),1.0]])]});}
            var Q4;
            {var subQ0=sQuery(id+"F0.wireOp",EDGE,"E42.0");var subQ1=sQuery(id+"F0.wireOp",EDGE,"E0.bottom");var subQ2=makeQuery(id+"F0.imprint","INTERSECT",VERTEX,{"derivedFrom":[subQ1,subQ0]});Q4=makeQuery(id+"F0.imprint","IMPRINT",FACE,{"disambiguationData":[TD([[makeQuery(id+"F0.imprint","IMPRINT",EDGE,{"disambiguationData":[TD([[subQ2,-1.0]])],"derivedFrom":subQ1}),1.0]])]});}
            extrude(context, id + "F4", {"entities" : qUnion([Q0, Q1, Q2, Q3, Q4]), "operationType" : NewBodyOperationType.REMOVE, "depth" : 1910 * mm, "offsetDistance" : 25 * mm, "hasSecondDirection" : true, "secondDirectionOppositeDirection" : false, "secondDirectionDepth" : 760 * mm});
        }
        {
            var Q0;
            {var subQ0=sQuery(id+"F0.wireOp",EDGE,"E10");var subQ1=sQuery(id+"F0.wireOp",EDGE,"E0.left");var subQ2=makeQuery(id+"F0.imprint","INTERSECT",VERTEX,{"derivedFrom":[subQ1,subQ0]});Q0=makeQuery(id+"F0.imprint","IMPRINT",FACE,{"disambiguationData":[TD([[makeQuery(id+"F0.imprint","IMPRINT",EDGE,{"disambiguationData":[TD([[subQ2,-1.0]])],"derivedFrom":subQ1}),-1.0]])]});}
            var Q1;
            {var subQ0=sQuery(id+"F0.wireOp",EDGE,"E17.0");var subQ1=sQuery(id+"F0.wireOp",EDGE,"E0.left");var subQ2=makeQuery(id+"F0.imprint","INTERSECT",VERTEX,{"derivedFrom":[subQ1,subQ0]});Q1=makeQuery(id+"F0.imprint","IMPRINT",FACE,{"disambiguationData":[TD([[makeQuery(id+"F0.imprint","IMPRINT",EDGE,{"disambiguationData":[TD([[subQ2,-1.0]])],"derivedFrom":subQ1}),-1.0]])]});}
            extrude(context, id + "F5", {"entities" : qUnion([Q0, Q1]), "operationType" : NewBodyOperationType.REMOVE, "depth" : 1910 * mm, "offsetDistance" : 25 * mm, "hasSecondDirection" : true, "secondDirectionOppositeDirection" : false, "secondDirectionDepth" : 1140 * mm});
        }
    });
